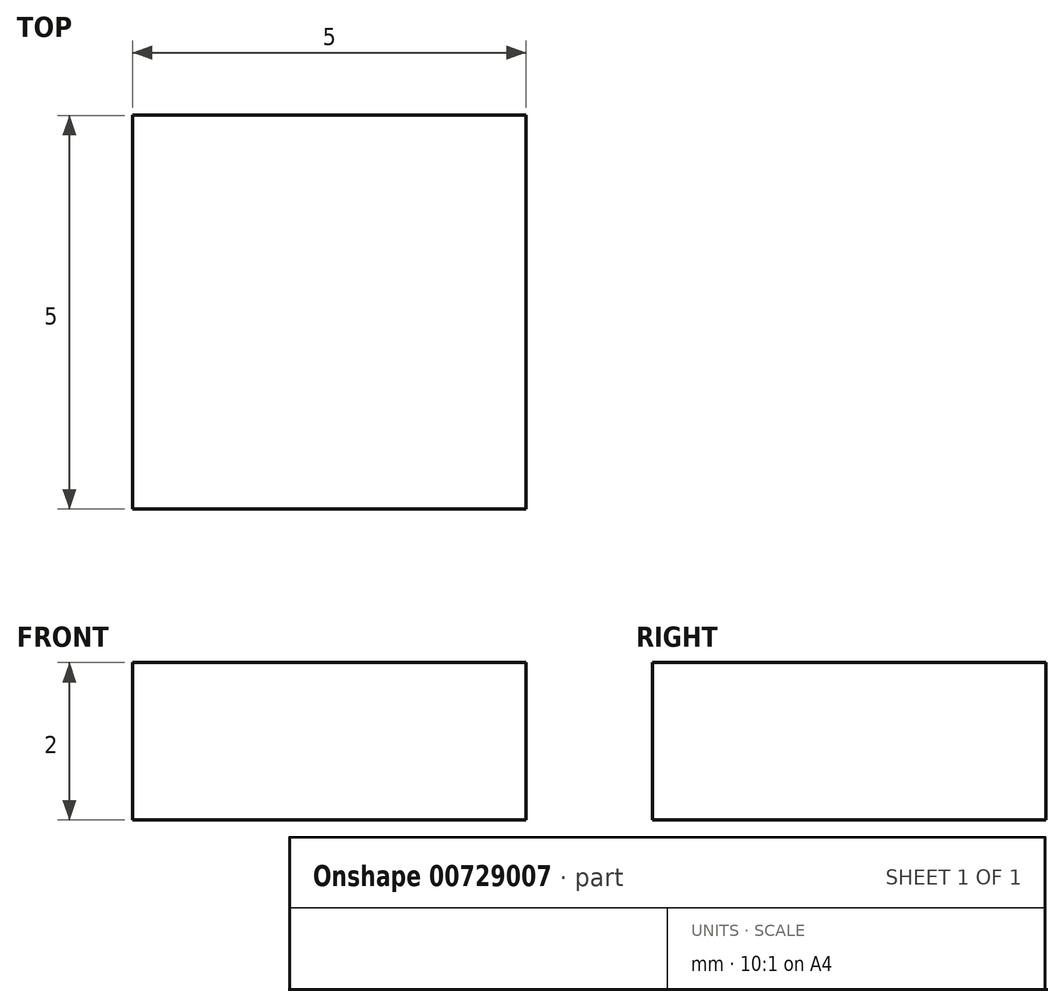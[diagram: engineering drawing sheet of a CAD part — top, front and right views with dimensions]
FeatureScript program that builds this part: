
annotation { "Feature Type Name" : "Feature", "Feature Type Description" : "" }
export const myFeature = defineFeature(function(context is Context, id is Id, definition is map)
    precondition{}
    {
        {
            var Q0;
            Q0=qCreatedBy(makeId("Top.planeOp"),FACE);
            var sketch = newSketch(context, id + "F0", { "sketchPlane" : qUnion([Q0])});
            skLineSegment(sketch, "E0.bottom", {"start": v(-2.27, 3) * mm, "end": v(2.73, 3) * mm});
            skLineSegment(sketch, "E0.top", {"start": v(-2.27, -2) * mm, "end": v(2.73, -2) * mm});
            skLineSegment(sketch, "E0.left", {"start": v(-2.27, 3) * mm, "end": v(-2.27, -2) * mm});
            skLineSegment(sketch, "E0.right", {"start": v(2.73, 3) * mm, "end": v(2.73, -2) * mm});
            skSolve(sketch);
        }
        {
            var Q0;
            Q0 = qSketchRegion(id + "F0", true);
            extrude(context, id + "F1", {"entities" : qUnion([Q0]), "depth" : 2 * mm, "offsetDistance" : 25 * mm});
        }
    });
